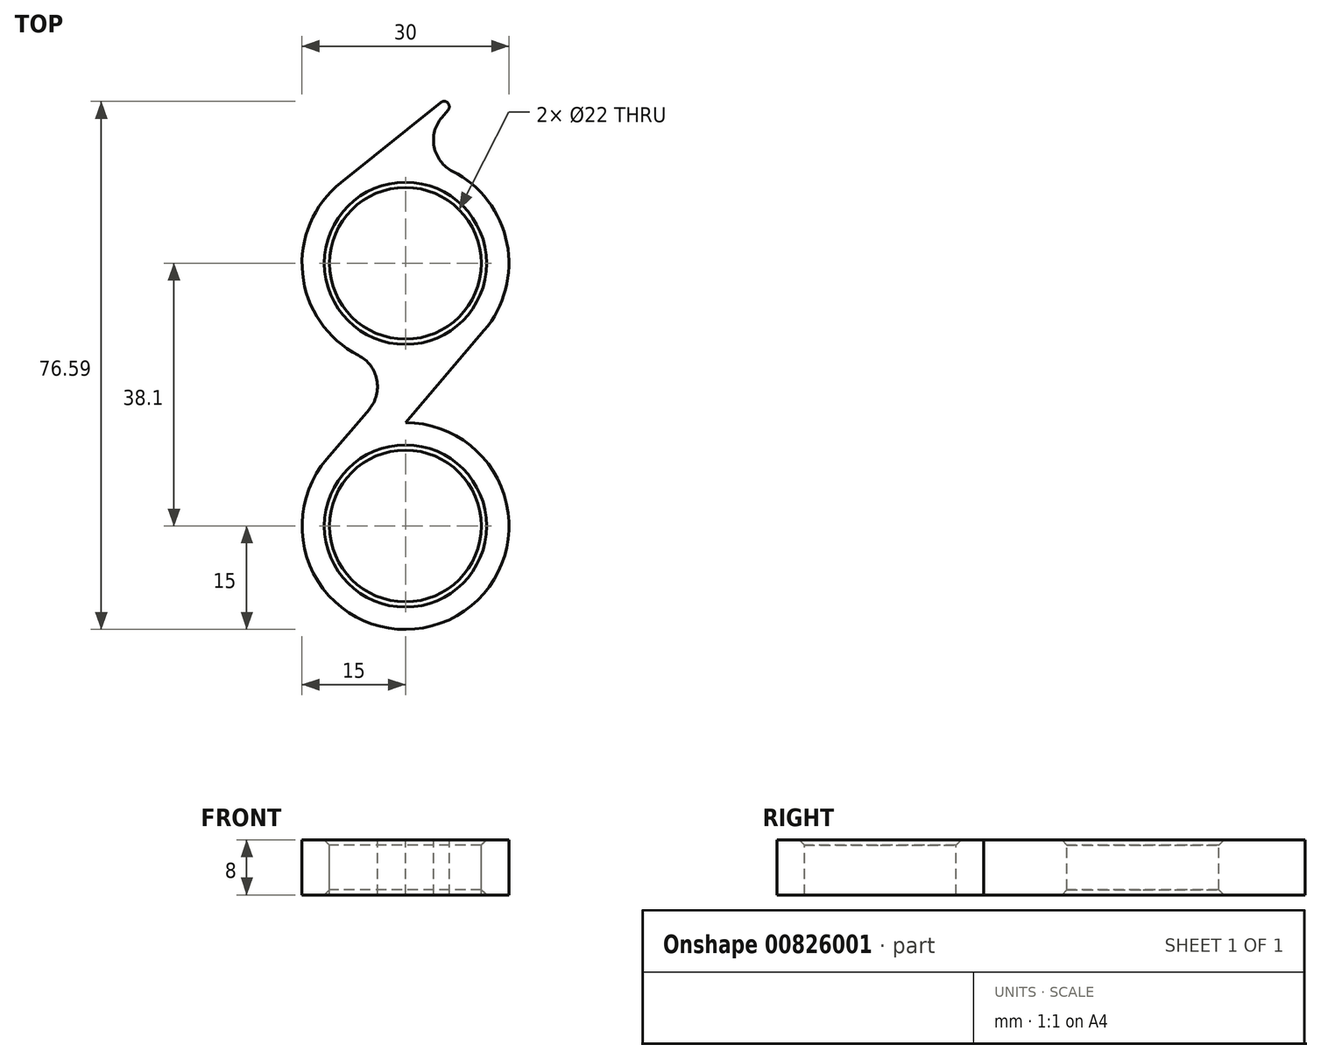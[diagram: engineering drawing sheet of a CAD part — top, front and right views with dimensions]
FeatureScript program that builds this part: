
annotation { "Feature Type Name" : "Feature", "Feature Type Description" : "" }
export const myFeature = defineFeature(function(context is Context, id is Id, definition is map)
    precondition{}
    {
        {
            var Q0;
            Q0=qCreatedBy(makeId("Top.planeOp"),FACE);
            var sketch = newSketch(context, id + "F0", { "sketchPlane" : qUnion([Q0])});
            skCircle(sketch, "E0", {"center": v(0, 0) * mm, "radius": 11 * mm});
            skCircle(sketch, "E1", {"center": v(0, 0) * mm, "radius": 15 * mm});
            skCircle(sketch, "E2", {"center": v(0, 38.1) * mm, "radius": 11 * mm});
            skCircle(sketch, "E3", {"center": v(0, 38.1) * mm, "radius": 15 * mm});
            skLineSegment(sketch, "E4", {"start": v(0, 23.1) * mm, "end": v(-11.4, 9.74) * mm});
            skLineSegment(sketch, "E5", {"start": v(0, 15) * mm, "end": v(11.4, 28.36) * mm});
            skLineSegment(sketch, "E6", {"start": v(0, 53.1) * mm, "end": v(11.4, 66.46) * mm});
            skLineSegment(sketch, "E7", {"start": v(11.4, 66.46) * mm, "end": v(-9.38, 49.8) * mm});
            skSolve(sketch);
        }
        {
            var Q0;
            Q0=makeQuery(id+"F0.imprint","IMPRINT",FACE,{"disambiguationData":[TD([[makeQuery(id+"F0.imprint","IMPRINT",EDGE,{"derivedFrom":sQuery(id+"F0.wireOp",EDGE,"E0")}),-1.0]])]});
            extrude(context, id + "F1", {"entities" : qUnion([Q0]), "oppositeDirection" : true, "depth" : 8 * mm, "offsetDistance" : 25.4 * mm});
        }
        {
            var Q0;
            {var subQ0=sQuery(id+"F0.wireOp",EDGE,"E4");Q0=makeQuery(id+"F0.imprint","IMPRINT",FACE,{"disambiguationData":[TD([[makeQuery(id+"F0.imprint","IMPRINT",EDGE,{"derivedFrom":subQ0}),1.0]])]});}
            var Q1;
            Q1=makeQuery(id+"F0.imprint","IMPRINT",FACE,{"disambiguationData":[TD([[makeQuery(id+"F0.imprint","IMPRINT",EDGE,{"derivedFrom":sQuery(id+"F0.wireOp",EDGE,"E2")}),-1.0]])]});
            var Q2;
            {var subQ0=sQuery(id+"F0.wireOp",EDGE,"E6");Q2=makeQuery(id+"F0.imprint","IMPRINT",FACE,{"disambiguationData":[TD([[makeQuery(id+"F0.imprint","IMPRINT",EDGE,{"derivedFrom":subQ0}),1.0]])]});}
            var Q3;
            Q3=makeQuery(id+"F1.opExtrude","CAP_FACE",FACE,{"disambiguationData":[OSD([sQuery(id+"F0.wireOp",EDGE,"E0"),sQuery(id+"F0.wireOp",EDGE,"E1")])],"isStart":false});
            extrude(context, id + "F2", {"entities" : qUnion([Q0, Q1, Q2]), "operationType" : NewBodyOperationType.ADD, "endBound" : BoundingType.UP_TO_SURFACE, "oppositeDirection" : true, "depth" : 25.4 * mm, "endBoundEntityFace" : qUnion([Q3]), "offsetDistance" : 25.4 * mm});
        }
        {
            var Q0;
            Q0=makeQuery(id+"F5VjdlOPYnMvKE7_1.1.F2.opExtrude","SWEPT_EDGE",EDGE,{"disambiguationData":[OSD([sQuery(id+"F0.wireOp",EDGE,"E1"),sQuery(id+"F0.wireOp",EDGE,"E5")])]});
            var Q1;
            Q1=makeQuery(id+"F2.opExtrude","SWEPT_EDGE",EDGE,{"disambiguationData":[OSD([sQuery(id+"F0.wireOp",EDGE,"E1"),sQuery(id+"F0.wireOp",EDGE,"E5")])]});
            var Q2;
            Q2=makeQuery(id+"F5VjdlOPYnMvKE7_1.2.F2.opExtrude","SWEPT_EDGE",EDGE,{"disambiguationData":[OSD([sQuery(id+"F0.wireOp",EDGE,"E1"),sQuery(id+"F0.wireOp",EDGE,"E5")])]});
            var Q3;
            Q3=makeQuery(id+"F5VjdlOPYnMvKE7_1.2.F2.opExtrude","SWEPT_EDGE",EDGE,{"disambiguationData":[OSD([sQuery(id+"F0.wireOp",EDGE,"E3"),sQuery(id+"F0.wireOp",EDGE,"E4")])]});
            var Q4;
            Q4=makeQuery(id+"F5VjdlOPYnMvKE7_1.1.F2.opExtrude","SWEPT_EDGE",EDGE,{"disambiguationData":[OSD([sQuery(id+"F0.wireOp",EDGE,"E3"),sQuery(id+"F0.wireOp",EDGE,"E4")])]});
            var Q5;
            Q5=makeQuery(id+"F2.opExtrude","SWEPT_EDGE",EDGE,{"disambiguationData":[OSD([sQuery(id+"F0.wireOp",EDGE,"E3"),sQuery(id+"F0.wireOp",EDGE,"E4")])]});
            var Q6;
            Q6=makeQuery(id+"F2.opExtrude","SWEPT_EDGE",EDGE,{"disambiguationData":[OSD([sQuery(id+"F0.wireOp",EDGE,"E3"),sQuery(id+"F0.wireOp",EDGE,"E6")])]});
            var Q7;
            Q7=makeQuery(id+"F5VjdlOPYnMvKE7_1.1.F2.opExtrude","SWEPT_EDGE",EDGE,{"disambiguationData":[OSD([sQuery(id+"F0.wireOp",EDGE,"E3"),sQuery(id+"F0.wireOp",EDGE,"E6")])]});
            var Q8;
            Q8=makeQuery(id+"F5VjdlOPYnMvKE7_1.2.F2.opExtrude","SWEPT_EDGE",EDGE,{"disambiguationData":[OSD([sQuery(id+"F0.wireOp",EDGE,"E3"),sQuery(id+"F0.wireOp",EDGE,"E6")])]});
            fillet(context, id + "F3", {"entities" : qUnion([Q0, Q1, Q2, Q3, Q4, Q5, Q6, Q7, Q8]), "radius" : 5.08 * mm, "tangentPropagation" : true, "allowEdgeOverflow" : false});
        }
        {
            var Q0;
            Q0=makeQuery(id+"F5VjdlOPYnMvKE7_1.1.F2.opExtrude","SWEPT_EDGE",EDGE,{"disambiguationData":[OSD([sQuery(id+"F0.wireOp",EDGE,"E6"),sQuery(id+"F0.wireOp",EDGE,"E7")])]});
            var Q1;
            Q1=makeQuery(id+"F5VjdlOPYnMvKE7_1.2.F2.opExtrude","SWEPT_EDGE",EDGE,{"disambiguationData":[OSD([sQuery(id+"F0.wireOp",EDGE,"E6"),sQuery(id+"F0.wireOp",EDGE,"E7")])]});
            var Q2;
            Q2=makeQuery(id+"F2.opExtrude","SWEPT_EDGE",EDGE,{"disambiguationData":[OSD([sQuery(id+"F0.wireOp",EDGE,"E6"),sQuery(id+"F0.wireOp",EDGE,"E7")])]});
            fillet(context, id + "F4", {"entities" : qUnion([Q0, Q1, Q2]), "radius" : 0.76 * mm, "tangentPropagation" : true, "allowEdgeOverflow" : false});
        }
        {
            var Q0;
            Q0=makeQuery(id+"F5VjdlOPYnMvKE7_1.2.F2.opExtrude","CAP_EDGE",EDGE,{"disambiguationData":[OSD([sQuery(id+"F0.wireOp",EDGE,"E2")])],"isStart":true});
            var Q1;
            Q1=makeQuery(id+"F5VjdlOPYnMvKE7_1.1.F2.opExtrude","CAP_EDGE",EDGE,{"disambiguationData":[OSD([sQuery(id+"F0.wireOp",EDGE,"E2")])],"isStart":true});
            var Q2;
            Q2=makeQuery(id+"F1.opExtrude","CAP_EDGE",EDGE,{"disambiguationData":[OSD([sQuery(id+"F0.wireOp",EDGE,"E0")])],"isStart":true});
            var Q3;
            Q3=makeQuery(id+"F2.opExtrude","CAP_EDGE",EDGE,{"disambiguationData":[OSD([sQuery(id+"F0.wireOp",EDGE,"E2")])],"isStart":true});
            var Q4;
            Q4=makeQuery(id+"F2.opExtrude","CAP_EDGE",EDGE,{"disambiguationData":[OSD([sQuery(id+"F0.wireOp",EDGE,"E2")])],"isStart":false});
            var Q5;
            Q5=makeQuery(id+"F5VjdlOPYnMvKE7_1.2.F2.opExtrude","CAP_EDGE",EDGE,{"disambiguationData":[OSD([sQuery(id+"F0.wireOp",EDGE,"E2")])],"isStart":false});
            var Q6;
            Q6=makeQuery(id+"F5VjdlOPYnMvKE7_1.1.F2.opExtrude","CAP_EDGE",EDGE,{"disambiguationData":[OSD([sQuery(id+"F0.wireOp",EDGE,"E2")])],"isStart":false});
            chamfer(context, id + "F5", {"entities" : qUnion([Q0, Q1, Q2, Q3, Q4, Q5, Q6]), "width" : 0.76 * mm, "tangentPropagation" : true});
        }
    });
